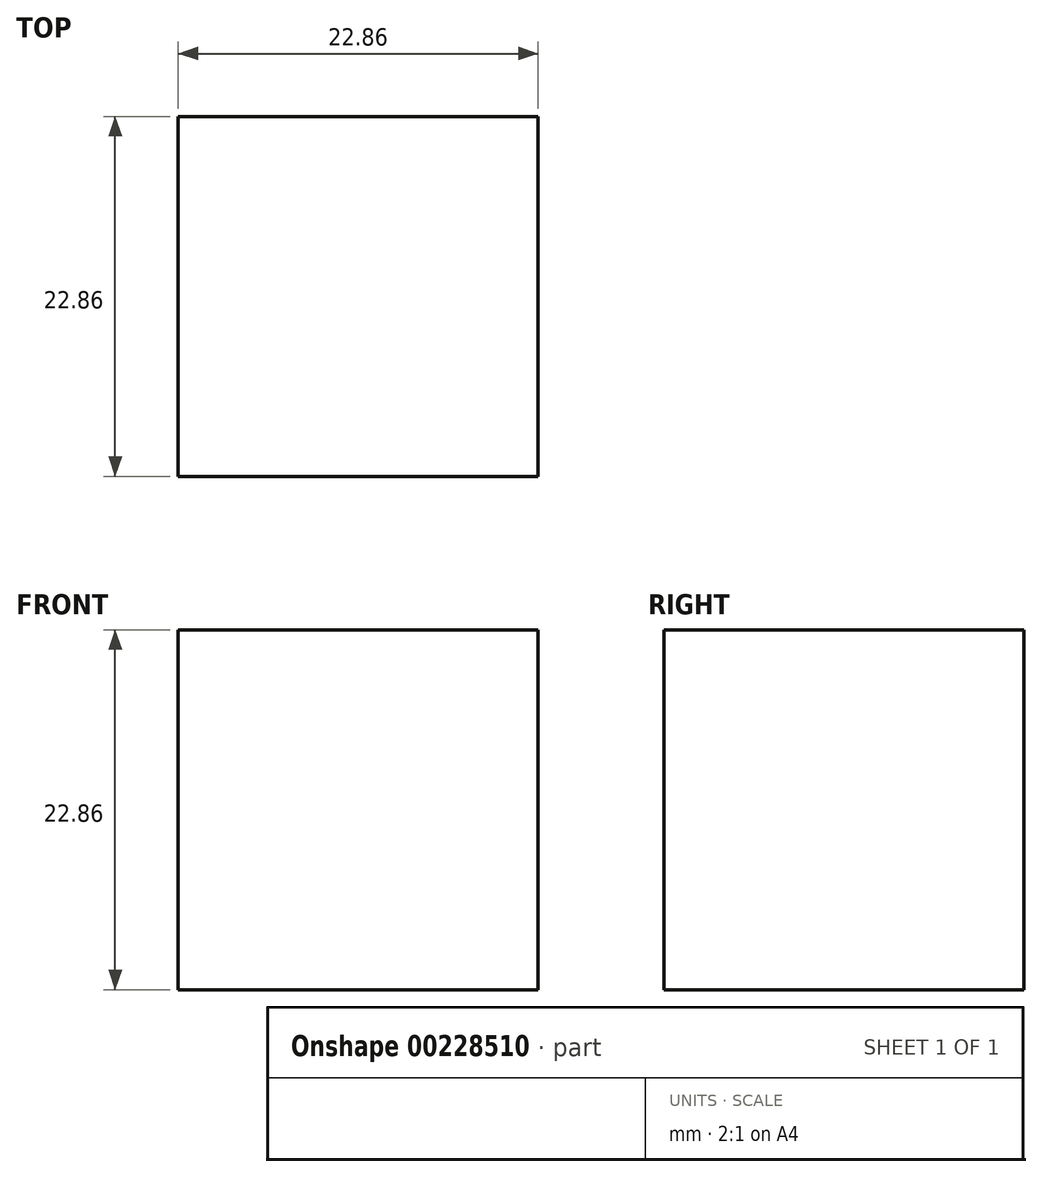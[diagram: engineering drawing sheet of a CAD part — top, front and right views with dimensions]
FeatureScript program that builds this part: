
annotation { "Feature Type Name" : "Feature", "Feature Type Description" : "" }
export const myFeature = defineFeature(function(context is Context, id is Id, definition is map)
    precondition{}
    {
        {
            var Q0;
            Q0=qCreatedBy(makeId("Top.planeOp"),FACE);
            var sketch = newSketch(context, id + "F0", { "sketchPlane" : qUnion([Q0])});
            skLineSegment(sketch, "E0.bottom", {"start": v(-11.43, -11.43) * mm, "end": v(11.43, -11.43) * mm});
            skLineSegment(sketch, "E0.top", {"start": v(-11.43, 11.43) * mm, "end": v(11.43, 11.43) * mm});
            skLineSegment(sketch, "E0.left", {"start": v(-11.43, -11.43) * mm, "end": v(-11.43, 11.43) * mm});
            skLineSegment(sketch, "E0.right", {"start": v(11.43, -11.43) * mm, "end": v(11.43, 11.43) * mm});
            skPoint(sketch, "E0.middle", {"position": v(0, 0) * mm});
            skSolve(sketch);
        }
        {
            var Q0;
            Q0 = qSketchRegion(id + "F0", true);
            extrude(context, id + "F1", {"entities" : qUnion([Q0]), "endBound" : BoundingType.SYMMETRIC, "depth" : 22.86 * mm});
        }
    });
